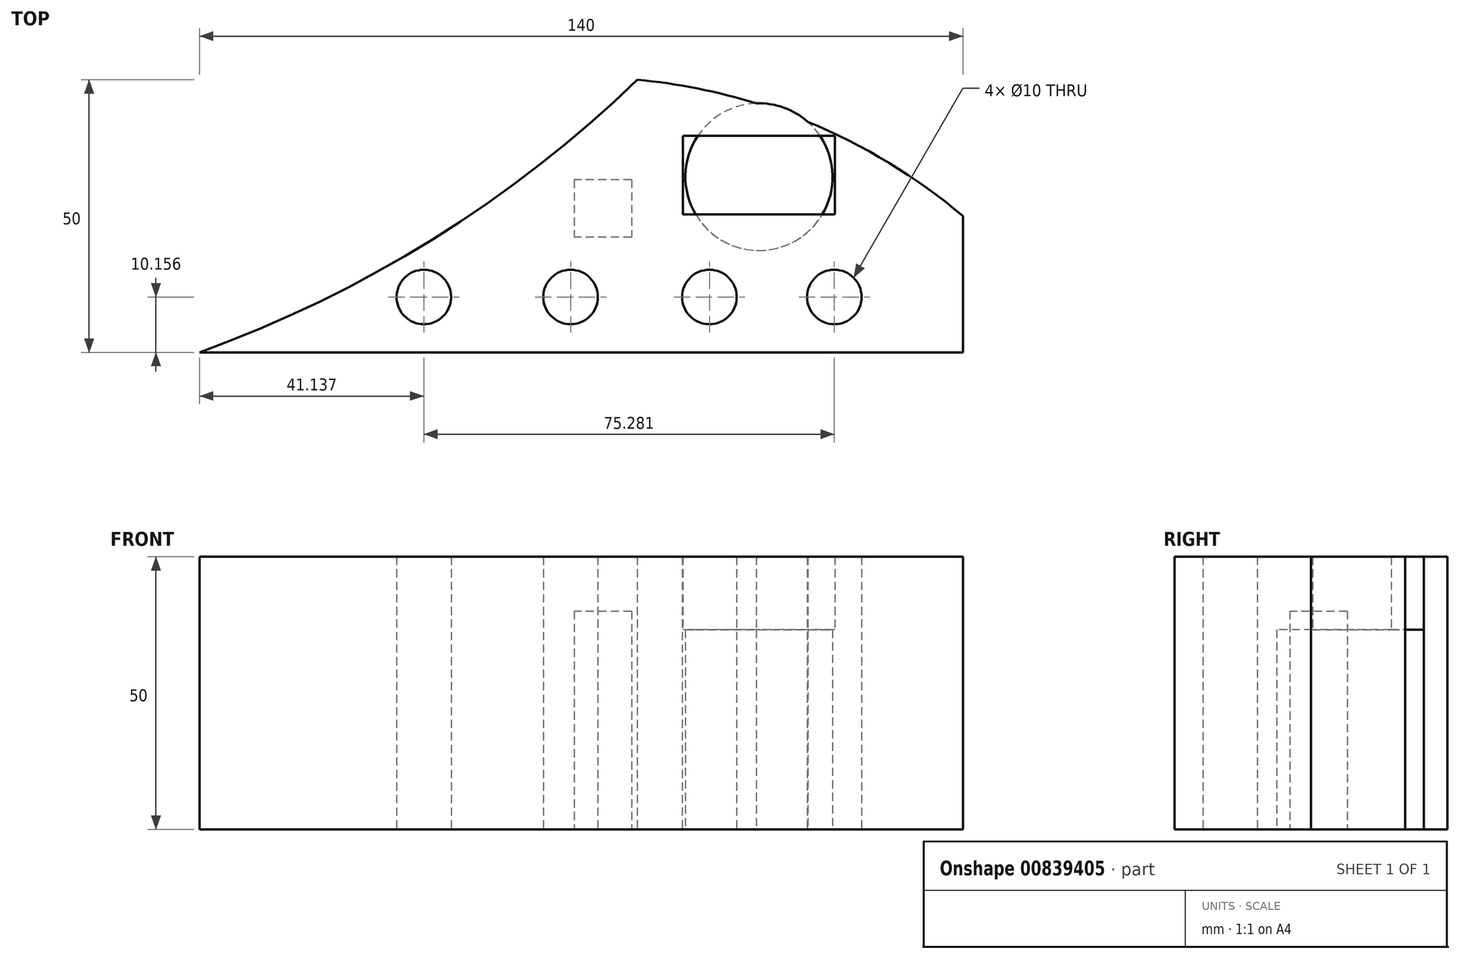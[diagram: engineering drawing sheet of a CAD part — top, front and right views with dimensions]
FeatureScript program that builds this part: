
annotation { "Feature Type Name" : "Feature", "Feature Type Description" : "" }
export const myFeature = defineFeature(function(context is Context, id is Id, definition is map)
    precondition{}
    {
        {
            var Q0;
            Q0=qCreatedBy(makeId("Top.planeOp"),FACE);
            var sketch = newSketch(context, id + "F0", { "sketchPlane" : qUnion([Q0])});
            skLineSegment(sketch, "E0.top", {"start": v(54, -43.2) * mm, "end": v(194, -43.2) * mm});
            skLineSegment(sketch, "E0.right", {"start": v(194, -18.2) * mm, "end": v(194, -43.2) * mm});
            skArc(sketch, "E1", {"start": v(54, -43.2) * mm, "mid": v(96.78, -22.44) * mm, "end": v(134.28, 6.8) * mm});
            skArc(sketch, "E2", {"start": v(194, -18.2) * mm, "mid": v(180.44, -8.45) * mm, "end": v(165.55, -0.9) * mm});
            skCircle(sketch, "E3", {"center": v(156.59, -11) * mm, "radius": 13.5 * mm});
            skCircle(sketch, "E4", {"center": v(95.13, -33.04) * mm, "radius": 5 * mm});
            skCircle(sketch, "E5", {"center": v(122.04, -33.04) * mm, "radius": 5 * mm});
            skCircle(sketch, "E6", {"center": v(147.5, -33.04) * mm, "radius": 5 * mm});
            skCircle(sketch, "E7", {"center": v(170.4, -33.04) * mm, "radius": 5 * mm});
            skPoint(sketch, "E0.bottom.end.orphan", {"position": v(194, 6.8) * mm});
            skArc(sketch, "E8.trimOffspring", {"start": v(156.1, 2.49) * mm, "mid": v(145.3, 5.2) * mm, "end": v(134.28, 6.8) * mm});
            skSolve(sketch);
        }
        {
            var Q0;
            Q0 = qSketchRegion(id + "F0", true);
            extrude(context, id + "F1", {"entities" : qUnion([Q0]), "depth" : 50 * mm, "offsetDistance" : 25 * mm});
        }
        {
            var Q0;
            {var subQ0=sQuery(id+"F0.wireOp",EDGE,"E3");var subQ1=makeQuery(id+"F0.imprint","INTERSECT",VERTEX,{"derivedFrom":[sQuery(id+"F0.wireOp",EDGE,"E2"),subQ0]});Q0=makeQuery(id+"F0.imprint","IMPRINT",FACE,{"disambiguationData":[TD([[makeQuery(id+"F0.imprint","IMPRINT",EDGE,{"disambiguationData":[TD([[subQ1,-1.0]])],"derivedFrom":subQ0}),1.0]])]});}
            extrude(context, id + "F2", {"entities" : qUnion([Q0]), "operationType" : NewBodyOperationType.REMOVE, "depth" : 36.6 * mm, "offsetDistance" : 25 * mm});
        }
        {
            var Q0;
            Q0=makeQuery(id+"F2.boolean.opBoolean","COPY",FACE,{"derivedFrom":makeQuery(id+"F2.opExtrude","CAP_FACE",FACE,{"disambiguationData":[OSD([sQuery(id+"F0.wireOp",EDGE,"E3")])],"isStart":false})});
            var sketch = newSketch(context, id + "F3", { "sketchPlane" : qUnion([Q0])});
            skCircle(sketch, "E9", {"center": v(156.59, 11) * mm, "radius": 4.8 * mm});
            skSolve(sketch);
        }
        {
            var Q0;
            Q0=makeQuery(id+"F3.imprint","IMPRINT",FACE,{"disambiguationData":[TD([[makeQuery(id+"F3.imprint","IMPRINT",EDGE,{"derivedFrom":sQuery(id+"F3.wireOp",EDGE,"E9")}),1.0]])]});
            extrude(context, id + "F4", {"entities" : qUnion([Q0]), "operationType" : NewBodyOperationType.REMOVE, "oppositeDirection" : true, "depth" : 2.7 * mm, "offsetDistance" : 25 * mm});
        }
        {
            var Q0;
            Q0=makeQuery(id+"F0.imprint","IMPRINT",FACE,{"disambiguationData":[TD([[makeQuery(id+"F0.imprint","IMPRINT",EDGE,{"derivedFrom":sQuery(id+"F0.wireOp",EDGE,"E0.top")}),1.0]])]});
            var sketch = newSketch(context, id + "F5", { "sketchPlane" : qUnion([Q0])});
            skLineSegment(sketch, "E10.bottom", {"start": v(133.21, -11.56) * mm, "end": v(122.71, -11.56) * mm});
            skLineSegment(sketch, "E10.top", {"start": v(133.21, -22.06) * mm, "end": v(122.71, -22.06) * mm});
            skLineSegment(sketch, "E10.left", {"start": v(133.21, -11.56) * mm, "end": v(133.21, -22.06) * mm});
            skLineSegment(sketch, "E10.right", {"start": v(122.71, -11.56) * mm, "end": v(122.71, -22.06) * mm});
            skSolve(sketch);
        }
        {
            var Q0;
            Q0 = qSketchRegion(id + "F5", true);
            extrude(context, id + "F6", {"entities" : qUnion([Q0]), "operationType" : NewBodyOperationType.REMOVE, "depth" : 40 * mm, "offsetDistance" : 25 * mm});
        }
        {
            var Q0;
            Q0=makeQuery(id+"F3.imprint","IMPRINT",FACE,{"disambiguationData":[TD([[makeQuery(id+"F3.imprint","IMPRINT",EDGE,{"derivedFrom":sQuery(id+"F3.wireOp",EDGE,"E9")}),-1.0]])]});
            var sketch = newSketch(context, id + "F7", { "sketchPlane" : qUnion([Q0])});
            skLineSegment(sketch, "E11.bottom", {"start": v(170.54, 3.47) * mm, "end": v(142.64, 3.47) * mm});
            skLineSegment(sketch, "E11.top", {"start": v(170.54, 17.91) * mm, "end": v(142.64, 17.91) * mm});
            skLineSegment(sketch, "E11.left", {"start": v(170.54, 3.47) * mm, "end": v(170.54, 17.91) * mm});
            skLineSegment(sketch, "E11.right", {"start": v(142.64, 3.47) * mm, "end": v(142.64, 17.91) * mm});
            skSolve(sketch);
        }
        {
            var Q0;
            Q0 = qSketchRegion(id + "F7", true);
            extrude(context, id + "F8", {"entities" : qUnion([Q0]), "operationType" : NewBodyOperationType.REMOVE, "oppositeDirection" : true, "depth" : 25 * mm, "offsetDistance" : 25 * mm});
        }
    });
